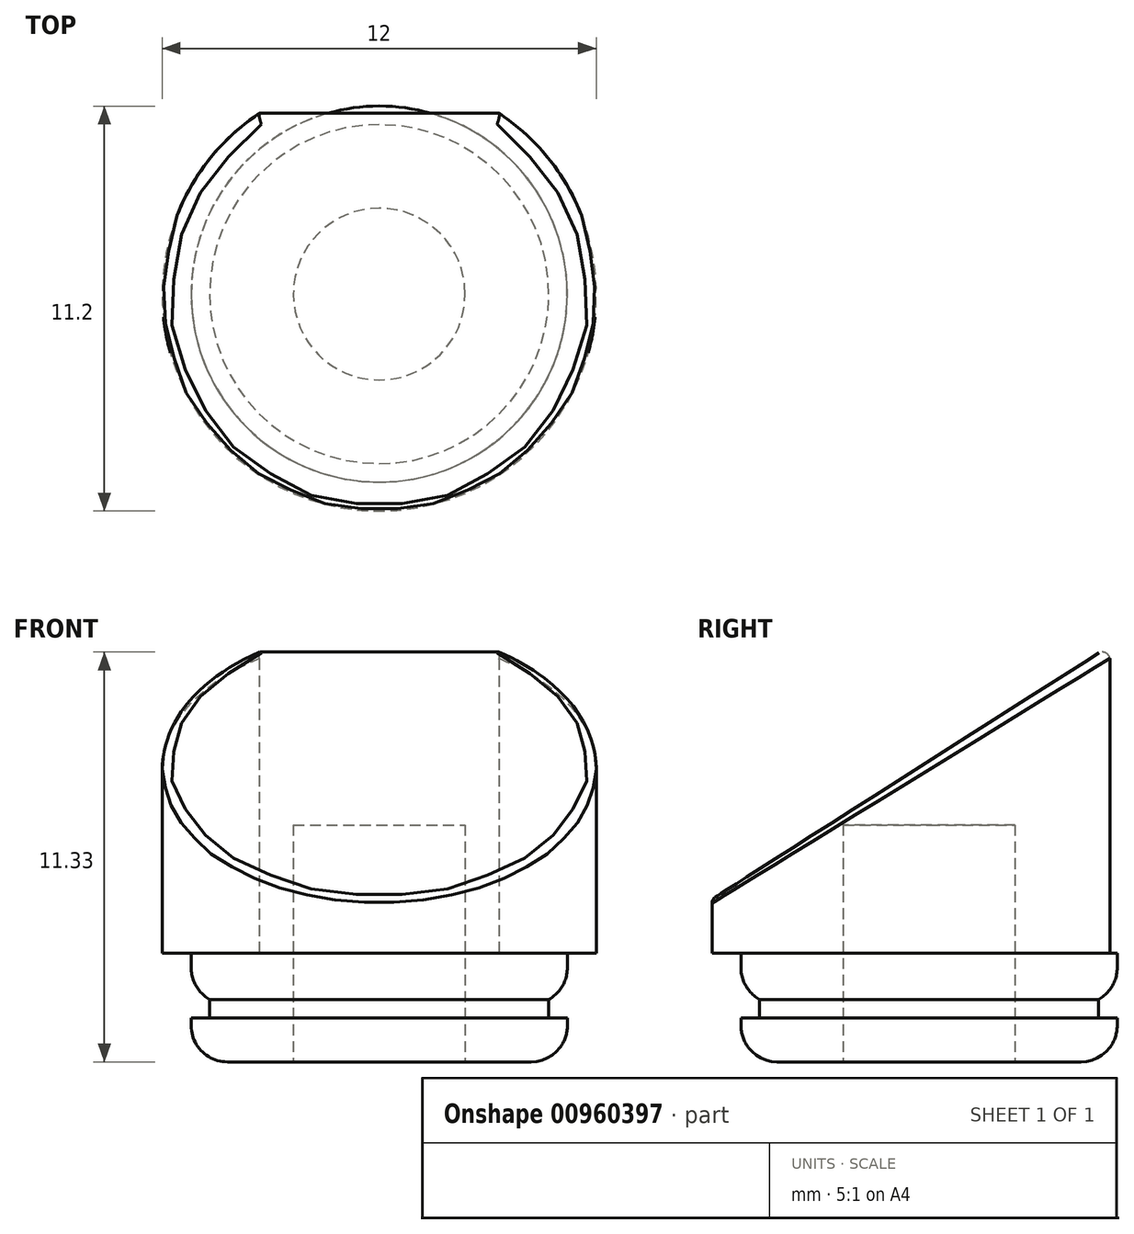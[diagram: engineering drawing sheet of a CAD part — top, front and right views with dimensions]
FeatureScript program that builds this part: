
annotation { "Feature Type Name" : "Feature", "Feature Type Description" : "" }
export const myFeature = defineFeature(function(context is Context, id is Id, definition is map)
    precondition{}
    {
        {
            var Q0;
            Q0=qCreatedBy(makeId("Top.planeOp"),FACE);
            var sketch = newSketch(context, id + "F0", { "sketchPlane" : qUnion([Q0])});
            skArc(sketch, "E0", {"start": v(-3.32, 5) * mm, "mid": v(0, -6) * mm, "end": v(3.32, 5) * mm});
            skLineSegment(sketch, "E1", {"start": v(-3.32, 5) * mm, "end": v(3.32, 5) * mm});
            skSolve(sketch);
        }
        {
            var Q0;
            Q0 = qSketchRegion(id + "F0", true);
            extrude(context, id + "F1", {"entities" : qUnion([Q0]), "depth" : 8.5 * mm, "offsetDistance" : 25 * mm});
        }
        {
            var Q0;
            Q0=qCreatedBy(makeId("Right.planeOp"),FACE);
            var sketch = newSketch(context, id + "F2", { "sketchPlane" : qUnion([Q0])});
            skLineSegment(sketch, "E2", {"start": v(5, 8.5) * mm, "end": v(-6, 1.5) * mm});
            skLineSegment(sketch, "E3", {"start": v(5, 8.5) * mm, "end": v(-6, 8.5) * mm});
            skLineSegment(sketch, "E4", {"start": v(-6, 8.5) * mm, "end": v(-6, 1.5) * mm});
            skPoint(sketch, "E5.end.orphan", {"position": v(-6, 0) * mm});
            skSolve(sketch);
        }
        {
            var Q0;
            Q0 = qSketchRegion(id + "F2", true);
            extrude(context, id + "F3", {"entities" : qUnion([Q0]), "operationType" : NewBodyOperationType.REMOVE, "oppositeDirection" : true, "depth" : 25 * mm, "offsetDistance" : 25 * mm, "hasSecondDirection" : true, "secondDirectionOppositeDirection" : false, "secondDirectionDepth" : 25 * mm});
        }
        {
            var Q0;
            Q0=makeQuery(id+"F1.opExtrude","CAP_FACE",FACE,{"disambiguationData":[OSD([sQuery(id+"F0.wireOp",EDGE,"E0"),sQuery(id+"F0.wireOp",EDGE,"E1")])],"isStart":true});
            var sketch = newSketch(context, id + "F4", { "sketchPlane" : qUnion([Q0])});
            skCircle(sketch, "E6", {"center": v(0, 0) * mm, "radius": 5.2 * mm});
            skSolve(sketch);
        }
        {
            var Q0;
            Q0 = qSketchRegion(id + "F4", true);
            extrude(context, id + "F5", {"entities" : qUnion([Q0]), "operationType" : NewBodyOperationType.ADD, "depth" : 3 * mm, "offsetDistance" : 25 * mm});
        }
        {
            var Q0;
            Q0=qCreatedBy(makeId("Front.planeOp"),FACE);
            var sketch = newSketch(context, id + "F6", { "sketchPlane" : qUnion([Q0])});
            skLineSegment(sketch, "E7.bottom", {"start": v(5.25, -1.27) * mm, "end": v(4.69, -1.27) * mm});
            skLineSegment(sketch, "E7.top", {"start": v(5.25, -1.79) * mm, "end": v(4.69, -1.79) * mm});
            skLineSegment(sketch, "E7.left", {"start": v(5.25, -1.27) * mm, "end": v(5.25, -1.79) * mm});
            skLineSegment(sketch, "E7.right", {"start": v(4.69, -1.27) * mm, "end": v(4.69, -1.79) * mm});
            skSolve(sketch);
        }
        {
            var Q0;
            Q0 = qSketchRegion(id + "F6", true);
            var Q1;
            Q1=makeQuery(id+"F5.opExtrude","SWEPT_FACE",FACE,{"disambiguationData":[OSD([sQuery(id+"F4.wireOp",EDGE,"E6")])]});
            revolve(context, id + "F7", {"operationType" : NewBodyOperationType.REMOVE, "surfaceOperationType" : NewSurfaceOperationType.NEW, "entities" : qUnion([Q0]), "axis" : qUnion([Q1]), "revolveType" : RevolveType.FULL});
        }
        {
            var Q0;
            Q0=makeQuery(id+"F5.opExtrude","CAP_EDGE",EDGE,{"disambiguationData":[OSD([sQuery(id+"F4.wireOp",EDGE,"E6")])],"isStart":false});
            fillet(context, id + "F8", {"entities" : qUnion([Q0]), "radius" : 1 * mm, "tangentPropagation" : true, "allowEdgeOverflow" : false});
        }
        {
            var Q0;
            Q0=makeQuery(id+"F7.boolean.opBoolean","INTERSECT",EDGE,{"derivedFrom":[makeQuery(id+"F5.opExtrude","SWEPT_FACE",FACE,{"disambiguationData":[OSD([sQuery(id+"F4.wireOp",EDGE,"E6")])]}),makeQuery(id+"F7.opRevolve","SWEPT_FACE",FACE,{"disambiguationData":[OSD([sQuery(id+"F6.wireOp",EDGE,"E7.bottom")])]})]});
            fillet(context, id + "F9", {"entities" : qUnion([Q0]), "radius" : 1 * mm, "tangentPropagation" : true, "allowEdgeOverflow" : false});
        }
        {
            var Q0;
            Q0=makeQuery(id+"F5.opExtrude","CAP_FACE",FACE,{"disambiguationData":[OSD([sQuery(id+"F4.wireOp",EDGE,"E6")])],"isStart":false});
            var sketch = newSketch(context, id + "F10", { "sketchPlane" : qUnion([Q0])});
            skCircle(sketch, "E8", {"center": v(0, 0) * mm, "radius": 2.38 * mm});
            skSolve(sketch);
        }
        {
            var Q0;
            Q0 = qSketchRegion(id + "F10", true);
            extrude(context, id + "F11", {"entities" : qUnion([Q0]), "operationType" : NewBodyOperationType.REMOVE, "oppositeDirection" : true, "depth" : 6.55 * mm, "offsetDistance" : 25 * mm});
        }
        {
            var Q0;
            Q0=makeQuery(id+"F3.boolean.opBoolean","MERGE",EDGE,{"derivedFrom":[makeQuery(id+"F1.opExtrude","CAP_EDGE",EDGE,{"disambiguationData":[OSD([sQuery(id+"F0.wireOp",EDGE,"E1")])],"isStart":false})],"fromTools":[makeQuery(id+"F3.opExtrude","SWEPT_EDGE",EDGE,{"disambiguationData":[OSD([sQuery(id+"F2.wireOp",EDGE,"E2"),sQuery(id+"F2.wireOp",EDGE,"E3")])]})]});
            var Q1;
            Q1=makeQuery(id+"F3.boolean.opBoolean","INTERSECT",EDGE,{"derivedFrom":[makeQuery(id+"F1.opExtrude","SWEPT_FACE",FACE,{"disambiguationData":[OSD([sQuery(id+"F0.wireOp",EDGE,"E0")])]}),makeQuery(id+"F3.opExtrude","SWEPT_FACE",FACE,{"disambiguationData":[OSD([sQuery(id+"F2.wireOp",EDGE,"E2")])]})]});
            fillet(context, id + "F12", {"entities" : qUnion([Q0, Q1]), "radius" : 0.2 * mm, "tangentPropagation" : true, "allowEdgeOverflow" : false});
        }
    });
